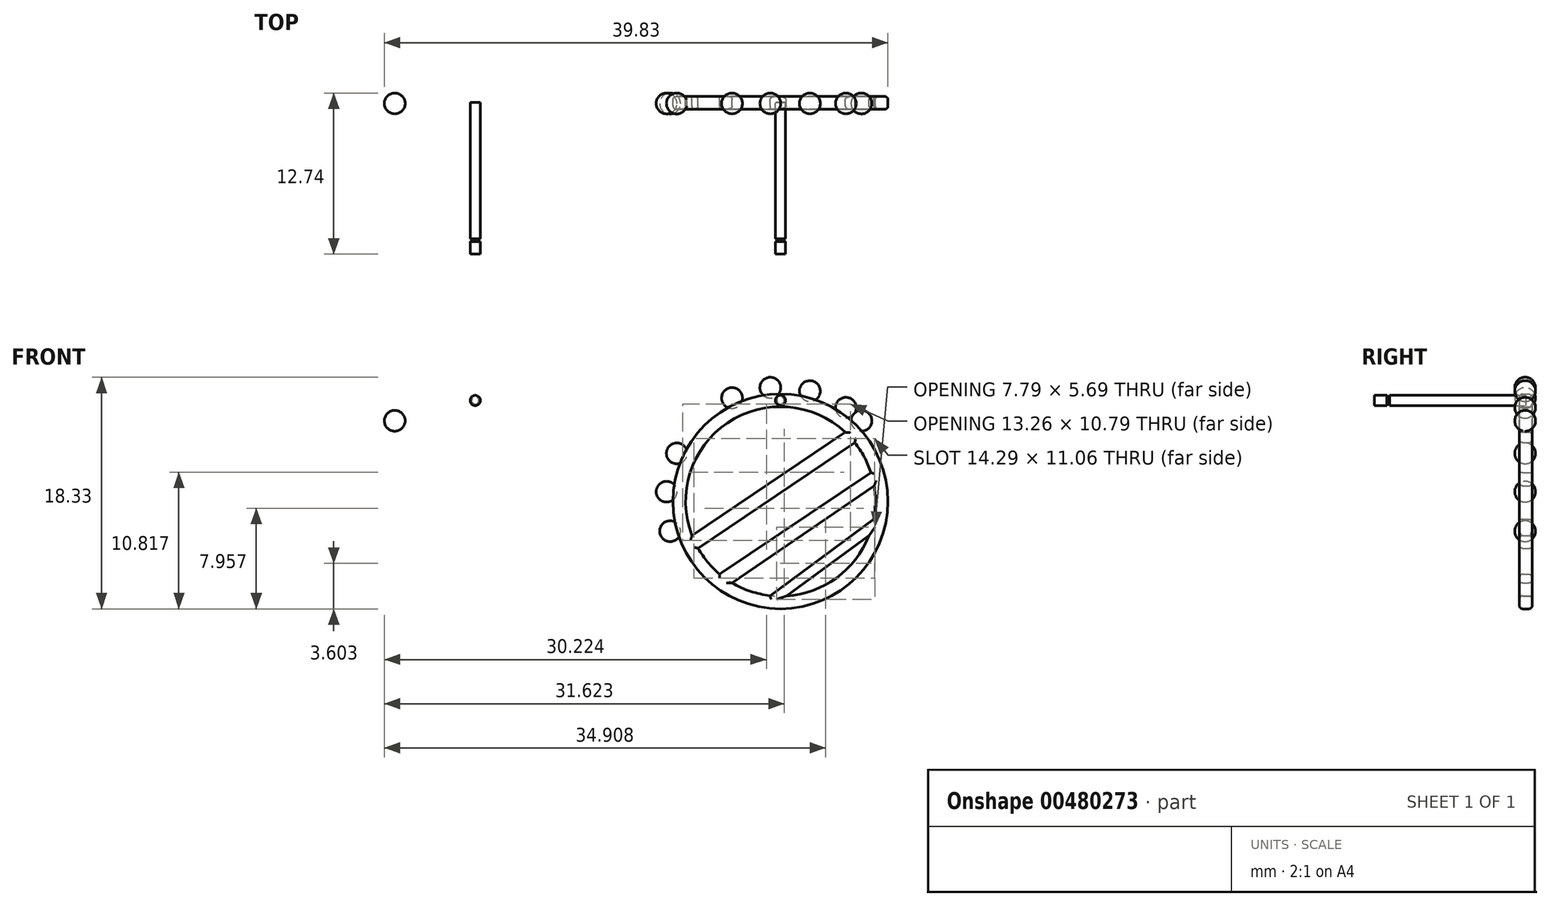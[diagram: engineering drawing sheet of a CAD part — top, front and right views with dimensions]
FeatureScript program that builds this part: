
annotation { "Feature Type Name" : "Feature", "Feature Type Description" : "" }
export const myFeature = defineFeature(function(context is Context, id is Id, definition is map)
    precondition{}
    {
        {
            var Q0;
            Q0=qCreatedBy(makeId("Front.planeOp"),FACE);
            var sketch = newSketch(context, id + "F0", { "sketchPlane" : qUnion([Q0])});
            skCircle(sketch, "E0", {"center": v(0, 0) * mm, "radius": 7.5 * mm});
            skCircle(sketch, "E1", {"center": v(0, 0) * mm, "radius": 8.5 * mm});
            skLineSegment(sketch, "E2", {"start": v(-7, -2.7) * mm, "end": v(5.13, 5.47) * mm});
            skLineSegment(sketch, "E3", {"start": v(-6.52, -3.7) * mm, "end": v(5.88, 4.65) * mm});
            skLineSegment(sketch, "E4", {"start": v(-4.8, -5.76) * mm, "end": v(7.14, 2.29) * mm});
            skLineSegment(sketch, "E5", {"start": v(-3.82, -6.46) * mm, "end": v(7.4, 1.23) * mm});
            skLineSegment(sketch, "E6", {"start": v(-0.83, -7.45) * mm, "end": v(7.37, -1.42) * mm});
            skLineSegment(sketch, "E7", {"start": v(0.46, -7.49) * mm, "end": v(7, -2.71) * mm});
            skSolve(sketch);
        }
        {
            var Q0;
            Q0=makeQuery(id+"F0.imprint","IMPRINT",FACE,{"disambiguationData":[TD([[makeQuery(id+"F0.imprint","IMPRINT",EDGE,{"derivedFrom":sQuery(id+"F0.wireOp",EDGE,"E0")}),-1.0]])]});
            var Q1;
            {var subQ0=sQuery(id+"F0.wireOp",EDGE,"E4");Q1=makeQuery(id+"F0.imprint","IMPRINT",FACE,{"disambiguationData":[TD([[makeQuery(id+"F0.imprint","IMPRINT",EDGE,{"derivedFrom":subQ0}),-1.0]])]});}
            var Q2;
            {var subQ0=sQuery(id+"F0.wireOp",EDGE,"E2");Q2=makeQuery(id+"F0.imprint","IMPRINT",FACE,{"disambiguationData":[TD([[makeQuery(id+"F0.imprint","IMPRINT",EDGE,{"derivedFrom":subQ0}),-1.0]])]});}
            var Q3;
            {var subQ0=sQuery(id+"F0.wireOp",EDGE,"E6");Q3=makeQuery(id+"F0.imprint","IMPRINT",FACE,{"disambiguationData":[TD([[makeQuery(id+"F0.imprint","IMPRINT",EDGE,{"derivedFrom":subQ0}),-1.0]])]});}
            extrude(context, id + "F1", {"entities" : qUnion([Q0, Q1, Q2, Q3]), "depth" : 1 * mm});
        }
        {
            var Q0;
            {var subQ0=sQuery(id+"F0.wireOp",EDGE,"E0");Q0=makeQuery(id+"F1.opExtrude","CAP_EDGE",EDGE,{"disambiguationData":[OSD([subQ0]),TDD([makeQuery(id+"F0.imprint","IMPRINT",EDGE,{"disambiguationData":[TD([[makeQuery(id+"F0.imprint","INTERSECT",VERTEX,{"disambiguationData":[OD(1.0)],"derivedFrom":[subQ0,sQuery(id+"F0.wireOp",EDGE,"E3")]}),1.0]])],"derivedFrom":subQ0})])],"isStart":true});}
            var Q1;
            {var subQ0=sQuery(id+"F0.wireOp",EDGE,"E2");var subQ1=sQuery(id+"F0.wireOp",EDGE,"E0");Q1=makeQuery(id+"F1.opExtrude","CAP_EDGE",EDGE,{"disambiguationData":[OSD([subQ1]),TDD([makeQuery(id+"F0.imprint","IMPRINT",EDGE,{"disambiguationData":[TD([[makeQuery(id+"F0.imprint","INTERSECT",VERTEX,{"disambiguationData":[OD(0.0)],"derivedFrom":[subQ1,subQ0]}),1.0]])],"derivedFrom":subQ1})])],"isStart":true});}
            var Q2;
            {var subQ0=sQuery(id+"F0.wireOp",EDGE,"E0");Q2=makeQuery(id+"F1.opExtrude","CAP_EDGE",EDGE,{"disambiguationData":[OSD([subQ0]),TDD([makeQuery(id+"F0.imprint","IMPRINT",EDGE,{"disambiguationData":[TD([[makeQuery(id+"F0.imprint","INTERSECT",VERTEX,{"disambiguationData":[OD(0.0)],"derivedFrom":[subQ0,sQuery(id+"F0.wireOp",EDGE,"E3")]}),-1.0]])],"derivedFrom":subQ0})])],"isStart":true});}
            var Q3;
            {var subQ0=sQuery(id+"F0.wireOp",EDGE,"E7");var subQ1=sQuery(id+"F0.wireOp",EDGE,"E0");Q3=makeQuery(id+"F1.opExtrude","CAP_EDGE",EDGE,{"disambiguationData":[OSD([subQ1]),TDD([makeQuery(id+"F0.imprint","IMPRINT",EDGE,{"disambiguationData":[TD([[makeQuery(id+"F0.imprint","INTERSECT",VERTEX,{"disambiguationData":[OD(0.0)],"derivedFrom":[subQ1,subQ0]}),-1.0]])],"derivedFrom":subQ1})])],"isStart":true});}
            var Q4;
            Q4=makeQuery(id+"F1.opExtrude","CAP_EDGE",EDGE,{"disambiguationData":[OSD([sQuery(id+"F0.wireOp",EDGE,"E1")])],"isStart":false});
            var Q5;
            Q5=makeQuery(id+"F1.opExtrude","CAP_EDGE",EDGE,{"disambiguationData":[OSD([sQuery(id+"F0.wireOp",EDGE,"E1")])],"isStart":true});
            var Q6;
            {var subQ0=sQuery(id+"F0.wireOp",EDGE,"E0");Q6=makeQuery(id+"F1.opExtrude","CAP_EDGE",EDGE,{"disambiguationData":[OSD([subQ0]),TDD([makeQuery(id+"F0.imprint","IMPRINT",EDGE,{"disambiguationData":[TD([[makeQuery(id+"F0.imprint","INTERSECT",VERTEX,{"disambiguationData":[OD(1.0)],"derivedFrom":[subQ0,sQuery(id+"F0.wireOp",EDGE,"E3")]}),1.0]])],"derivedFrom":subQ0})])],"isStart":false});}
            var Q7;
            {var subQ0=sQuery(id+"F0.wireOp",EDGE,"E2");var subQ1=sQuery(id+"F0.wireOp",EDGE,"E0");Q7=makeQuery(id+"F1.opExtrude","CAP_EDGE",EDGE,{"disambiguationData":[OSD([subQ1]),TDD([makeQuery(id+"F0.imprint","IMPRINT",EDGE,{"disambiguationData":[TD([[makeQuery(id+"F0.imprint","INTERSECT",VERTEX,{"disambiguationData":[OD(0.0)],"derivedFrom":[subQ1,subQ0]}),1.0]])],"derivedFrom":subQ1})])],"isStart":false});}
            var Q8;
            {var subQ0=sQuery(id+"F0.wireOp",EDGE,"E0");Q8=makeQuery(id+"F1.opExtrude","CAP_EDGE",EDGE,{"disambiguationData":[OSD([subQ0]),TDD([makeQuery(id+"F0.imprint","IMPRINT",EDGE,{"disambiguationData":[TD([[makeQuery(id+"F0.imprint","INTERSECT",VERTEX,{"disambiguationData":[OD(0.0)],"derivedFrom":[subQ0,sQuery(id+"F0.wireOp",EDGE,"E3")]}),-1.0]])],"derivedFrom":subQ0})])],"isStart":false});}
            var Q9;
            {var subQ0=sQuery(id+"F0.wireOp",EDGE,"E0");Q9=makeQuery(id+"F1.opExtrude","CAP_EDGE",EDGE,{"disambiguationData":[OSD([subQ0]),TDD([makeQuery(id+"F0.imprint","IMPRINT",EDGE,{"disambiguationData":[TD([[makeQuery(id+"F0.imprint","INTERSECT",VERTEX,{"disambiguationData":[OD(0.0)],"derivedFrom":[subQ0,sQuery(id+"F0.wireOp",EDGE,"E5")]}),-1.0]])],"derivedFrom":subQ0})])],"isStart":false});}
            var Q10;
            {var subQ0=sQuery(id+"F0.wireOp",EDGE,"E7");var subQ1=sQuery(id+"F0.wireOp",EDGE,"E0");Q10=makeQuery(id+"F1.opExtrude","CAP_EDGE",EDGE,{"disambiguationData":[OSD([subQ1]),TDD([makeQuery(id+"F0.imprint","IMPRINT",EDGE,{"disambiguationData":[TD([[makeQuery(id+"F0.imprint","INTERSECT",VERTEX,{"disambiguationData":[OD(0.0)],"derivedFrom":[subQ1,subQ0]}),-1.0]])],"derivedFrom":subQ1})])],"isStart":false});}
            var Q11;
            {var subQ0=sQuery(id+"F0.wireOp",EDGE,"E0");Q11=makeQuery(id+"F1.opExtrude","CAP_EDGE",EDGE,{"disambiguationData":[OSD([subQ0]),TDD([makeQuery(id+"F0.imprint","IMPRINT",EDGE,{"disambiguationData":[TD([[makeQuery(id+"F0.imprint","INTERSECT",VERTEX,{"disambiguationData":[OD(1.0)],"derivedFrom":[subQ0,sQuery(id+"F0.wireOp",EDGE,"E5")]}),1.0]])],"derivedFrom":subQ0})])],"isStart":false});}
            var Q12;
            Q12=makeQuery(id+"F1.opExtrude","CAP_EDGE",EDGE,{"disambiguationData":[OSD([sQuery(id+"F0.wireOp",EDGE,"E2")])],"isStart":false});
            var Q13;
            Q13=makeQuery(id+"F1.opExtrude","CAP_EDGE",EDGE,{"disambiguationData":[OSD([sQuery(id+"F0.wireOp",EDGE,"E3")])],"isStart":false});
            var Q14;
            Q14=makeQuery(id+"F1.opExtrude","CAP_EDGE",EDGE,{"disambiguationData":[OSD([sQuery(id+"F0.wireOp",EDGE,"E4")])],"isStart":false});
            var Q15;
            Q15=makeQuery(id+"F1.opExtrude","CAP_EDGE",EDGE,{"disambiguationData":[OSD([sQuery(id+"F0.wireOp",EDGE,"E5")])],"isStart":false});
            var Q16;
            Q16=makeQuery(id+"F1.opExtrude","CAP_EDGE",EDGE,{"disambiguationData":[OSD([sQuery(id+"F0.wireOp",EDGE,"E6")])],"isStart":false});
            var Q17;
            Q17=makeQuery(id+"F1.opExtrude","CAP_EDGE",EDGE,{"disambiguationData":[OSD([sQuery(id+"F0.wireOp",EDGE,"E7")])],"isStart":false});
            var Q18;
            Q18=makeQuery(id+"F1.opExtrude","CAP_EDGE",EDGE,{"disambiguationData":[OSD([sQuery(id+"F0.wireOp",EDGE,"E3")])],"isStart":true});
            var Q19;
            Q19=makeQuery(id+"F1.opExtrude","CAP_EDGE",EDGE,{"disambiguationData":[OSD([sQuery(id+"F0.wireOp",EDGE,"E2")])],"isStart":true});
            var Q20;
            Q20=makeQuery(id+"F1.opExtrude","CAP_EDGE",EDGE,{"disambiguationData":[OSD([sQuery(id+"F0.wireOp",EDGE,"E4")])],"isStart":true});
            var Q21;
            Q21=makeQuery(id+"F1.opExtrude","CAP_EDGE",EDGE,{"disambiguationData":[OSD([sQuery(id+"F0.wireOp",EDGE,"E7")])],"isStart":true});
            var Q22;
            Q22=makeQuery(id+"F1.opExtrude","CAP_EDGE",EDGE,{"disambiguationData":[OSD([sQuery(id+"F0.wireOp",EDGE,"E6")])],"isStart":true});
            var Q23;
            Q23=makeQuery(id+"F1.opExtrude","CAP_EDGE",EDGE,{"disambiguationData":[OSD([sQuery(id+"F0.wireOp",EDGE,"E5")])],"isStart":true});
            var Q24;
            {var subQ0=sQuery(id+"F0.wireOp",EDGE,"E0");Q24=makeQuery(id+"F1.opExtrude","CAP_EDGE",EDGE,{"disambiguationData":[OSD([subQ0]),TDD([makeQuery(id+"F0.imprint","IMPRINT",EDGE,{"disambiguationData":[TD([[makeQuery(id+"F0.imprint","INTERSECT",VERTEX,{"disambiguationData":[OD(1.0)],"derivedFrom":[subQ0,sQuery(id+"F0.wireOp",EDGE,"E5")]}),1.0]])],"derivedFrom":subQ0})])],"isStart":true});}
            fillet(context, id + "F2", {"entities" : qUnion([Q0, Q1, Q2, Q3, Q4, Q5, Q6, Q7, Q8, Q9, Q10, Q11, Q12, Q13, Q14, Q15, Q16, Q17, Q18, Q19, Q20, Q21, Q22, Q23, Q24]), "radius" : .25 * mm, "tangentPropagation" : true, "allowEdgeOverflow" : false});
        }
        {
            var Q0;
            Q0=qCreatedBy(makeId("Front.planeOp"),FACE);
            var sketch = newSketch(context, id + "F3", { "sketchPlane" : qUnion([Q0])});
            skCircle(sketch, "E8", {"center": v(-16.14, 6.84) * mm, "radius": 0.82 * mm});
            skLineSegment(sketch, "E9", {"start": v(-16.14, 9.43) * mm, "end": v(-16.14, 3.02) * mm});
            skSolve(sketch);
        }
        {
            var Q0;
            {var subQ0=sQuery(id+"F3.wireOp",EDGE,"E9");var subQ1=sQuery(id+"F3.wireOp",EDGE,"E8");var subQ2=makeQuery(id+"F3.imprint","INTERSECT",VERTEX,{"disambiguationData":[OD(0.0)],"derivedFrom":[subQ1,subQ0]});Q0=makeQuery(id+"F3.imprint","IMPRINT",FACE,{"disambiguationData":[TD([[makeQuery(id+"F3.imprint","IMPRINT",EDGE,{"disambiguationData":[TD([[subQ2,1.0]])],"derivedFrom":subQ1}),1.0]])]});}
            var Q1;
            Q1=sQuery(id+"F3.wireOp",EDGE,"E9");
            revolve(context, id + "F4", {"entities" : qUnion([Q0]), "axis" : qUnion([Q1]), "revolveType" : RevolveType.FULL});
        }
        {
            var Q0;
            Q0=makeQuery(id+"F4.opRevolve","SWEPT_BODY",BODY,{"disambiguationData":[OSD([sQuery(id+"F3.wireOp",EDGE,"E8"),sQuery(id+"F3.wireOp",EDGE,"E9")])]});
            transform(context, id + "F5", {"entities" : qUnion([Q0]), "transformType" : TransformType.TRANSLATION_3D, "dx" : 7.4 * mm, "dy" : -0.55 * mm, "dz" : -9.2 * mm, "makeCopy" : false});
        }
        {
            var Q0;
            Q0=makeQuery(id+"F4.opRevolve","SWEPT_BODY",BODY,{"disambiguationData":[OSD([sQuery(id+"F3.wireOp",EDGE,"E8"),sQuery(id+"F3.wireOp",EDGE,"E9")])]});
            var Q1;
            {var subQ0=sQuery(id+"F0.wireOp",EDGE,"E1");Q1=makeQuery(id+"F2.opFillet","BLEND_EDGE",EDGE,{"blendedFrom":[makeQuery(id+"F1.opExtrude","CAP_EDGE",EDGE,{"disambiguationData":[OSD([subQ0])],"isStart":false}),makeQuery(id+"F1.opExtrude","SWEPT_FACE",FACE,{"disambiguationData":[OSD([subQ0])]})],"blendedInto":[makeQuery(id+"F1.opExtrude","SWEPT_FACE",FACE,{"disambiguationData":[OSD([subQ0])]})]});}
            circularPattern(context, id + "F6", {"entities" : qUnion([Q0]), "axis" : qUnion([Q1]), "angle" : 140 * degree, "instanceCount" : 8, "oppositeDirection" : true, "equalSpace" : true});
        }
        {
            var Q0;
            Q0=makeQuery(id+"F6.opPattern","COPY",BODY,{"derivedFrom":makeQuery(id+"F4.opRevolve","SWEPT_BODY",BODY,{"disambiguationData":[OSD([sQuery(id+"F3.wireOp",EDGE,"E8"),sQuery(id+"F3.wireOp",EDGE,"E9")])]}),"instanceName":"3"});
            var Q1;
            Q1=qCreatedBy(makeId("Right.planeOp"),FACE);
            mirror(context, id + "F7", {"entities" : qUnion([Q0]), "mirrorPlane" : qUnion([Q1])});
        }
        {
            var Q0;
            Q0=makeQuery(id+"F6.opPattern","COPY",BODY,{"derivedFrom":makeQuery(id+"F4.opRevolve","SWEPT_BODY",BODY,{"disambiguationData":[OSD([sQuery(id+"F3.wireOp",EDGE,"E8"),sQuery(id+"F3.wireOp",EDGE,"E9")])]}),"instanceName":"3"});
            transform(context, id + "F8", {"entities" : qUnion([Q0]), "transformType" : TransformType.TRANSLATION_3D, "dx" : -24.1 * mm, "dy" : 0 * mm, "dz" : 0 * mm, "makeCopy" : false});
        }
        {
            var Q0;
            Q0=qCreatedBy(makeId("Front.planeOp"),FACE);
            var sketch = newSketch(context, id + "F9", { "sketchPlane" : qUnion([Q0])});
            skCircle(sketch, "E10", {"center": v(0, 0) * mm, "radius": 0.4 * mm});
            skSolve(sketch);
        }
        {
            var Q0;
            Q0=makeQuery(id+"F9.imprint","IMPRINT",FACE,{"disambiguationData":[TD([[makeQuery(id+"F9.imprint","IMPRINT",EDGE,{"derivedFrom":sQuery(id+"F9.wireOp",EDGE,"E10")}),1.0]])]});
            extrude(context, id + "F10", {"entities" : qUnion([Q0]), "depth" : 12 * mm});
        }
        {
            var Q0;
            Q0=qCreatedBy(makeId("Top.planeOp"),FACE);
            var sketch = newSketch(context, id + "F11", { "sketchPlane" : qUnion([Q0])});
            skCircle(sketch, "E11", {"center": v(0.4, -10.9) * mm, "radius": 0.1 * mm});
            skSolve(sketch);
        }
        {
            var Q0;
            Q0 = qSketchRegion(id + "F11", true);
            var Q1;
            Q1=makeQuery(id+"F10.opExtrude","CAP_EDGE",EDGE,{"disambiguationData":[OSD([sQuery(id+"F9.wireOp",EDGE,"E10")])],"isStart":false});
            revolve(context, id + "F12", {"operationType" : NewBodyOperationType.REMOVE, "entities" : qUnion([Q0]), "axis" : qUnion([Q1]), "revolveType" : RevolveType.FULL, "oppositeDirection" : true});
        }
        {
            var Q0;
            Q0=makeQuery(id+"F10.opExtrude","SWEPT_BODY",BODY,{"disambiguationData":[OSD([sQuery(id+"F9.wireOp",EDGE,"E10")])]});
            transform(context, id + "F13", {"entities" : qUnion([Q0]), "transformType" : TransformType.COPY});
        }
        {
            var Q0;
            Q0=makeQuery(id+"F10.opExtrude","SWEPT_BODY",BODY,{"disambiguationData":[OSD([sQuery(id+"F9.wireOp",EDGE,"E10")])]});
            transform(context, id + "F14", {"entities" : qUnion([Q0]), "transformType" : TransformType.TRANSLATION_3D, "dx" : 0 * mm, "dy" : -0.47 * mm, "dz" : 8 * mm, "makeCopy" : false});
        }
        {
            var Q0;
            Q0=makeQuery(id+"F13.opPattern","COPY",BODY,{"derivedFrom":makeQuery(id+"F10.opExtrude","SWEPT_BODY",BODY,{"disambiguationData":[OSD([sQuery(id+"F9.wireOp",EDGE,"E10")])]}),"instanceName":"1"});
            transform(context, id + "F15", {"entities" : qUnion([Q0]), "transformType" : TransformType.TRANSLATION_3D, "dx" : -24.14 * mm, "dy" : -0.47 * mm, "dz" : 8 * mm, "makeCopy" : false});
        }
    });
